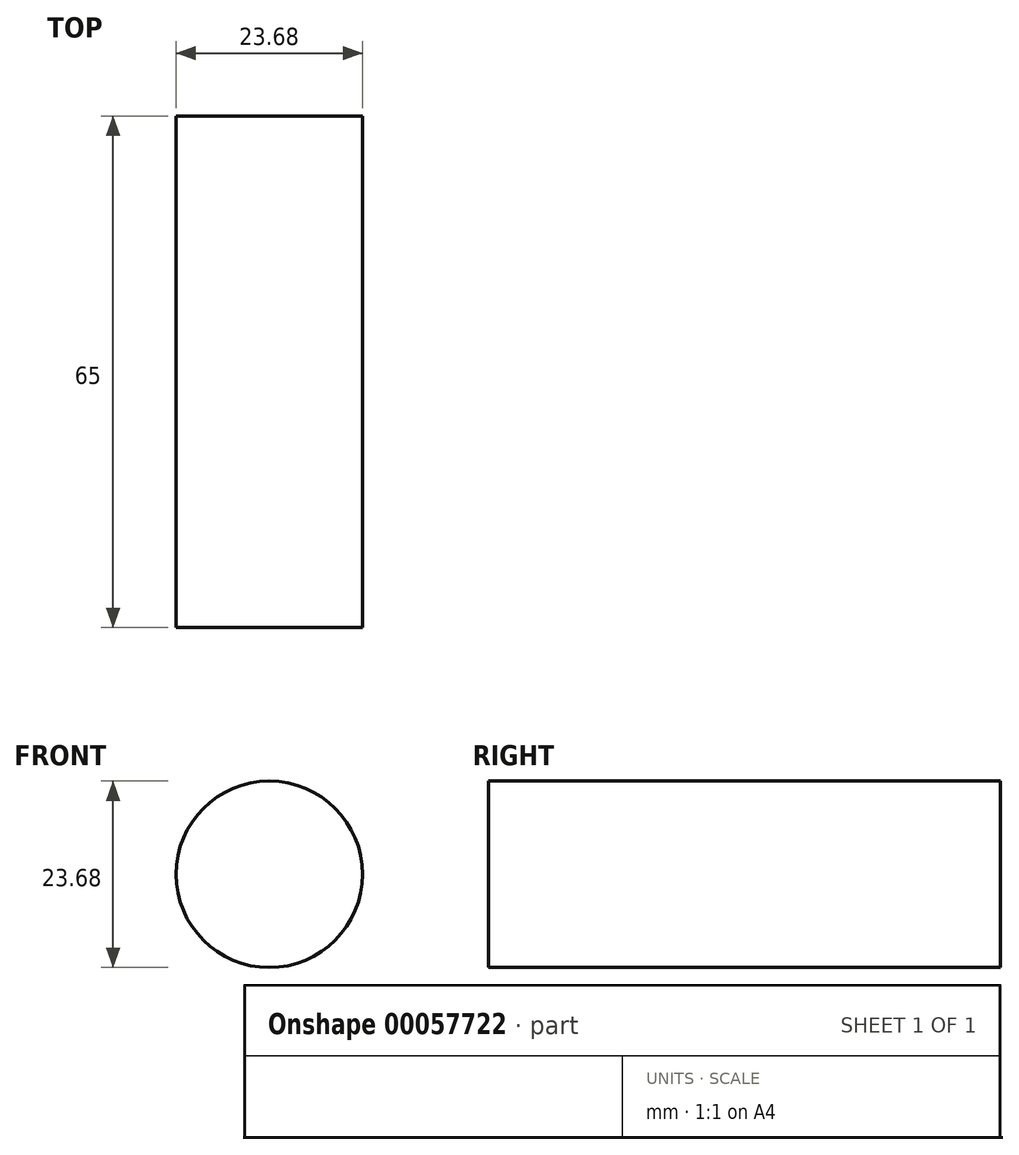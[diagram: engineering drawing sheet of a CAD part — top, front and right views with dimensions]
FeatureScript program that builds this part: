
annotation { "Feature Type Name" : "Feature", "Feature Type Description" : "" }
export const myFeature = defineFeature(function(context is Context, id is Id, definition is map)
    precondition{}
    {
        {
            var Q0;
            Q0=qCreatedBy(makeId("Front.planeOp"),FACE);
            var sketch = newSketch(context, id + "F0", { "sketchPlane" : qUnion([Q0])});
            skLineSegment(sketch, "E0.bottom", {"start": v(-63.86, 48.58) * mm, "end": v(-15.21, 48.58) * mm});
            skLineSegment(sketch, "E0.top", {"start": v(-63.86, 11.5) * mm, "end": v(-15.21, 11.5) * mm});
            skLineSegment(sketch, "E0.left", {"start": v(-63.86, 48.58) * mm, "end": v(-63.86, 11.5) * mm});
            skLineSegment(sketch, "E0.right", {"start": v(-15.21, 48.58) * mm, "end": v(-15.21, 11.5) * mm});
            skCircle(sketch, "E1", {"center": v(-41.23, 30.86) * mm, "radius": 11.84 * mm});
            skSolve(sketch);
        }
        {
            var Q0;
            Q0=sQuery(id+"F0.wireOp",EDGE,"E1");
            extrude(context, id + "F1", {"bodyType" : ToolBodyType.SURFACE, "surfaceEntities" : qUnion([Q0]), "depth" : 65 * mm});
        }
    });
